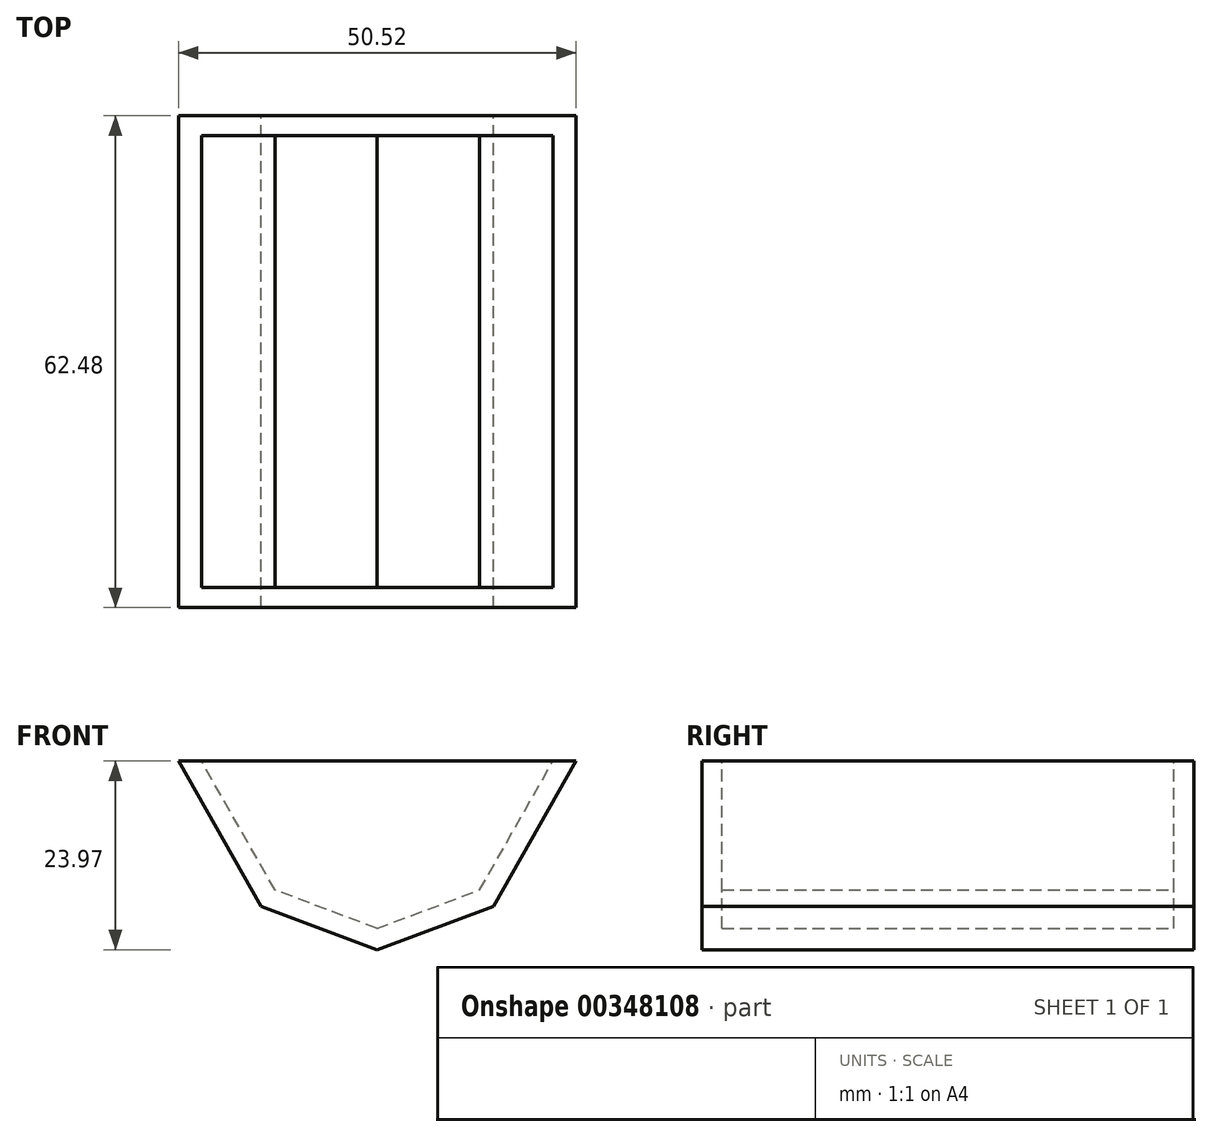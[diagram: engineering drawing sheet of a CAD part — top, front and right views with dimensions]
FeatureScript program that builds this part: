
annotation { "Feature Type Name" : "Feature", "Feature Type Description" : "" }
export const myFeature = defineFeature(function(context is Context, id is Id, definition is map)
    precondition{}
    {
        {
            var Q0;
            Q0=qCreatedBy(makeId("Front.planeOp"),FACE);
            var sketch = newSketch(context, id + "F0", { "sketchPlane" : qUnion([Q0])});
            skLineSegment(sketch, "E0", {"start": v(0, -23.97) * mm, "end": v(-14.75, -18.44) * mm});
            skLineSegment(sketch, "E1", {"start": v(-14.75, -18.44) * mm, "end": v(-25.26, 0) * mm});
            skLineSegment(sketch, "E2", {"start": v(-25.26, 0) * mm, "end": v(0, 0) * mm});
            skLineSegment(sketch, "E3.MirrorCS", {"start": v(25.26, 0) * mm, "end": v(0, 0) * mm});
            skLineSegment(sketch, "E4.MirrorCS", {"start": v(14.75, -18.44) * mm, "end": v(25.26, 0) * mm});
            skLineSegment(sketch, "E5.MirrorCS", {"start": v(0, -23.97) * mm, "end": v(14.75, -18.44) * mm});
            skSolve(sketch);
        }
        {
            var Q0;
            Q0 = qSketchRegion(id + "F0", true);
            extrude(context, id + "F1", {"entities" : qUnion([Q0]), "depth" : 62.48 * mm});
        }
        {
            var Q0;
            Q0=makeQuery(id+"F1.opExtrude","SWEPT_FACE",FACE,{"disambiguationData":[OSD([sQuery(id+"F0.wireOp",EDGE,"E2"),sQuery(id+"F0.wireOp",EDGE,"E3.MirrorCS")])]});
            shell(context, id + "F2", {"entities" : qUnion([Q0]), "thickness" : 2.54 * mm});
        }
        {
            var Q0;
            Q0=makeQuery(id+"F1.opExtrude","SWEPT_FACE",FACE,{"disambiguationData":[OSD([sQuery(id+"F0.wireOp",EDGE,"E2"),sQuery(id+"F0.wireOp",EDGE,"E3.MirrorCS")])]});
            cPlane(context, id + "F3", {"entities" : qUnion([Q0]), "cplaneType" : CPlaneType.OFFSET, "offset" : 25.4 * mm, "width" : 152.4 * mm, "height" : 152.4 * mm});
        }
    });
